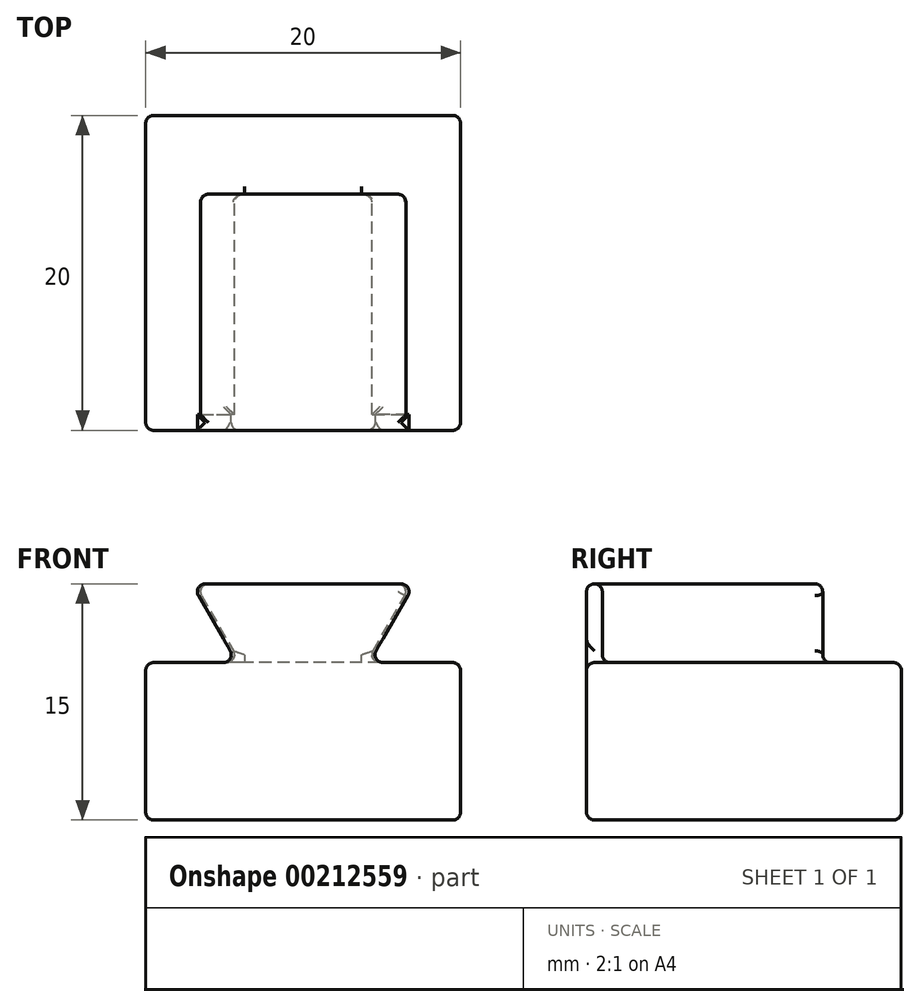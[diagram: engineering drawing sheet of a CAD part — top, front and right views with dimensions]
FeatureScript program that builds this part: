
annotation { "Feature Type Name" : "Feature", "Feature Type Description" : "" }
export const myFeature = defineFeature(function(context is Context, id is Id, definition is map)
    precondition{}
    {
        {
            var Q0;
            Q0=qCreatedBy(makeId("Front.planeOp"),FACE);
            var sketch = newSketch(context, id + "F0", { "sketchPlane" : qUnion([Q0])});
            skLineSegment(sketch, "E0", {"start": v(0, 0) * mm, "end": v(0, 10) * mm});
            skLineSegment(sketch, "E1", {"start": v(20, 10) * mm, "end": v(20, 0) * mm});
            skLineSegment(sketch, "E2", {"start": v(20, 0) * mm, "end": v(0, 0) * mm});
            skPoint(sketch, "E3.visualSharp", {"position": v(16.89, 15) * mm});
            skPoint(sketch, "E4.visualSharp", {"position": v(6, 10) * mm});
            skLineSegment(sketch, "E5", {"start": v(3.11, 15) * mm, "end": v(16.89, 15) * mm});
            skLineSegment(sketch, "E6", {"start": v(14, 10) * mm, "end": v(20, 10) * mm});
            skLineSegment(sketch, "E7", {"start": v(14, 10) * mm, "end": v(16.89, 15) * mm});
            skLineSegment(sketch, "E8", {"start": v(6, 10) * mm, "end": v(0, 10) * mm});
            skLineSegment(sketch, "E9", {"start": v(3.11, 15) * mm, "end": v(6, 10) * mm});
            skSolve(sketch);
        }
        {
            var Q0;
            Q0=makeQuery(id+"F0.imprint","IMPRINT",FACE,{"disambiguationData":[TD([[makeQuery(id+"F0.imprint","IMPRINT",EDGE,{"derivedFrom":sQuery(id+"F0.wireOp",EDGE,"E0")}),-1.0]])]});
            extrude(context, id + "F1", {"entities" : qUnion([Q0]), "oppositeDirection" : true, "depth" : 15 * mm});
        }
        {
            var Q0;
            Q0=makeQuery(id+"F1.opExtrude","CAP_FACE",FACE,{"disambiguationData":[OSD([sQuery(id+"F0.wireOp",EDGE,"E0"),sQuery(id+"F0.wireOp",EDGE,"E1"),sQuery(id+"F0.wireOp",EDGE,"E2"),sQuery(id+"F0.wireOp",EDGE,"E5"),sQuery(id+"F0.wireOp",EDGE,"E6"),sQuery(id+"F0.wireOp",EDGE,"E7"),sQuery(id+"F0.wireOp",EDGE,"E8"),sQuery(id+"F0.wireOp",EDGE,"E9")])],"isStart":false});
            var sketch = newSketch(context, id + "F2", { "sketchPlane" : qUnion([Q0])});
            skLineSegment(sketch, "E10.bottom", {"start": v(-20, 0) * mm, "end": v(0, 0) * mm});
            skLineSegment(sketch, "E10.top", {"start": v(-20, 10) * mm, "end": v(0, 10) * mm});
            skLineSegment(sketch, "E10.left", {"start": v(-20, 0) * mm, "end": v(-20, 10) * mm});
            skLineSegment(sketch, "E10.right", {"start": v(0, 0) * mm, "end": v(0, 10) * mm});
            skSolve(sketch);
        }
        {
            var Q0;
            Q0=qSketchRegion(id+"F2",true);
            extrude(context, id + "F3", {"entities" : qUnion([Q0]), "operationType" : NewBodyOperationType.ADD, "depth" : 5 * mm});
        }
        {
            var Q0;
            Q0=makeQuery(id+"F1.opExtrude","CAP_FACE",FACE,{"disambiguationData":[OSD([sQuery(id+"F0.wireOp",EDGE,"E0"),sQuery(id+"F0.wireOp",EDGE,"E1"),sQuery(id+"F0.wireOp",EDGE,"E2"),sQuery(id+"F0.wireOp",EDGE,"E5"),sQuery(id+"F0.wireOp",EDGE,"E6"),sQuery(id+"F0.wireOp",EDGE,"E7"),sQuery(id+"F0.wireOp",EDGE,"E8"),sQuery(id+"F0.wireOp",EDGE,"E9")])],"isStart":true});
            var sketch = newSketch(context, id + "F4", { "sketchPlane" : qUnion([Q0])});
            skLineSegment(sketch, "E11", {"start": v(3.11, 15) * mm, "end": v(2.91, 15) * mm});
            skLineSegment(sketch, "E12", {"start": v(2.91, 15) * mm, "end": v(5.8, 10) * mm});
            skLineSegment(sketch, "E13", {"start": v(5.8, 10) * mm, "end": v(6, 10) * mm});
            skLineSegment(sketch, "E14", {"start": v(6, 10) * mm, "end": v(3.11, 15) * mm});
            skLineSegment(sketch, "E15", {"start": v(16.89, 15) * mm, "end": v(17.09, 15) * mm});
            skLineSegment(sketch, "E16", {"start": v(17.09, 15) * mm, "end": v(14.2, 10) * mm});
            skLineSegment(sketch, "E17", {"start": v(14.2, 10) * mm, "end": v(14, 10) * mm});
            skLineSegment(sketch, "E18", {"start": v(14, 10) * mm, "end": v(16.89, 15) * mm});
            skSolve(sketch);
        }
        {
            var Q0;
            Q0 = qSketchRegion(id + "F4", true);
            extrude(context, id + "F5", {"entities" : qUnion([Q0]), "operationType" : NewBodyOperationType.ADD, "oppositeDirection" : true, "depth" : 1 * mm});
        }
        {
            var Q0;
            Q0=makeQuery(id+"F5.boolean.opBoolean","MERGE",FACE,{"derivedFrom":[makeQuery(id+"F1.opExtrude","SWEPT_FACE",FACE,{"disambiguationData":[OSD([sQuery(id+"F0.wireOp",EDGE,"E5")])]}),makeQuery(id+"F5.opExtrude","SWEPT_FACE",FACE,{"disambiguationData":[OSD([sQuery(id+"F4.wireOp",EDGE,"E11")])]}),makeQuery(id+"F5.opExtrude","SWEPT_FACE",FACE,{"disambiguationData":[OSD([sQuery(id+"F4.wireOp",EDGE,"E15")])]})]});
            var Q1;
            Q1=makeQuery(id+"F3.boolean.opBoolean","MERGE",FACE,{"derivedFrom":[makeQuery(id+"F1.opExtrude","SWEPT_FACE",FACE,{"disambiguationData":[OSD([sQuery(id+"F0.wireOp",EDGE,"E6")])]}),makeQuery(id+"F1.opExtrude","SWEPT_FACE",FACE,{"disambiguationData":[OSD([sQuery(id+"F0.wireOp",EDGE,"E8")])]}),makeQuery(id+"F3.opExtrude","SWEPT_FACE",FACE,{"disambiguationData":[OSD([sQuery(id+"F2.wireOp",EDGE,"E10.top")])]})]});
            var Q2;
            Q2=makeQuery(id+"F3.boolean.opBoolean","MERGE",FACE,{"derivedFrom":[makeQuery(id+"F1.opExtrude","SWEPT_FACE",FACE,{"disambiguationData":[OSD([sQuery(id+"F0.wireOp",EDGE,"E2")])]}),makeQuery(id+"F3.opExtrude","SWEPT_FACE",FACE,{"disambiguationData":[OSD([sQuery(id+"F2.wireOp",EDGE,"E10.bottom")])]})]});
            var Q3;
            Q3=makeQuery(id+"F1.opExtrude","CAP_EDGE",EDGE,{"disambiguationData":[OSD([sQuery(id+"F0.wireOp",EDGE,"E0")])],"isStart":true});
            var Q4;
            Q4=makeQuery(id+"F1.opExtrude","CAP_EDGE",EDGE,{"disambiguationData":[OSD([sQuery(id+"F0.wireOp",EDGE,"E1")])],"isStart":true});
            var Q5;
            Q5=makeQuery(id+"F3.opExtrude","CAP_EDGE",EDGE,{"disambiguationData":[OSD([sQuery(id+"F2.wireOp",EDGE,"E10.right")])],"isStart":false});
            var Q6;
            Q6=makeQuery(id+"F3.opExtrude","CAP_EDGE",EDGE,{"disambiguationData":[OSD([sQuery(id+"F2.wireOp",EDGE,"E10.left")])],"isStart":false});
            var Q7;
            Q7=makeQuery(id+"F1.opExtrude","CAP_EDGE",EDGE,{"disambiguationData":[OSD([sQuery(id+"F0.wireOp",EDGE,"E9")])],"isStart":false});
            var Q8;
            Q8=makeQuery(id+"F1.opExtrude","CAP_EDGE",EDGE,{"disambiguationData":[OSD([sQuery(id+"F0.wireOp",EDGE,"E7")])],"isStart":false});
            fillet(context, id + "F6", {"entities" : qUnion([Q0, Q1, Q2, Q3, Q4, Q5, Q6, Q7, Q8]), "radius" : 0.5 * mm, "tangentPropagation" : true, "defaultsChanged" : false, "vertexSettings" : [], "allowEdgeOverflow" : false});
        }
    });
